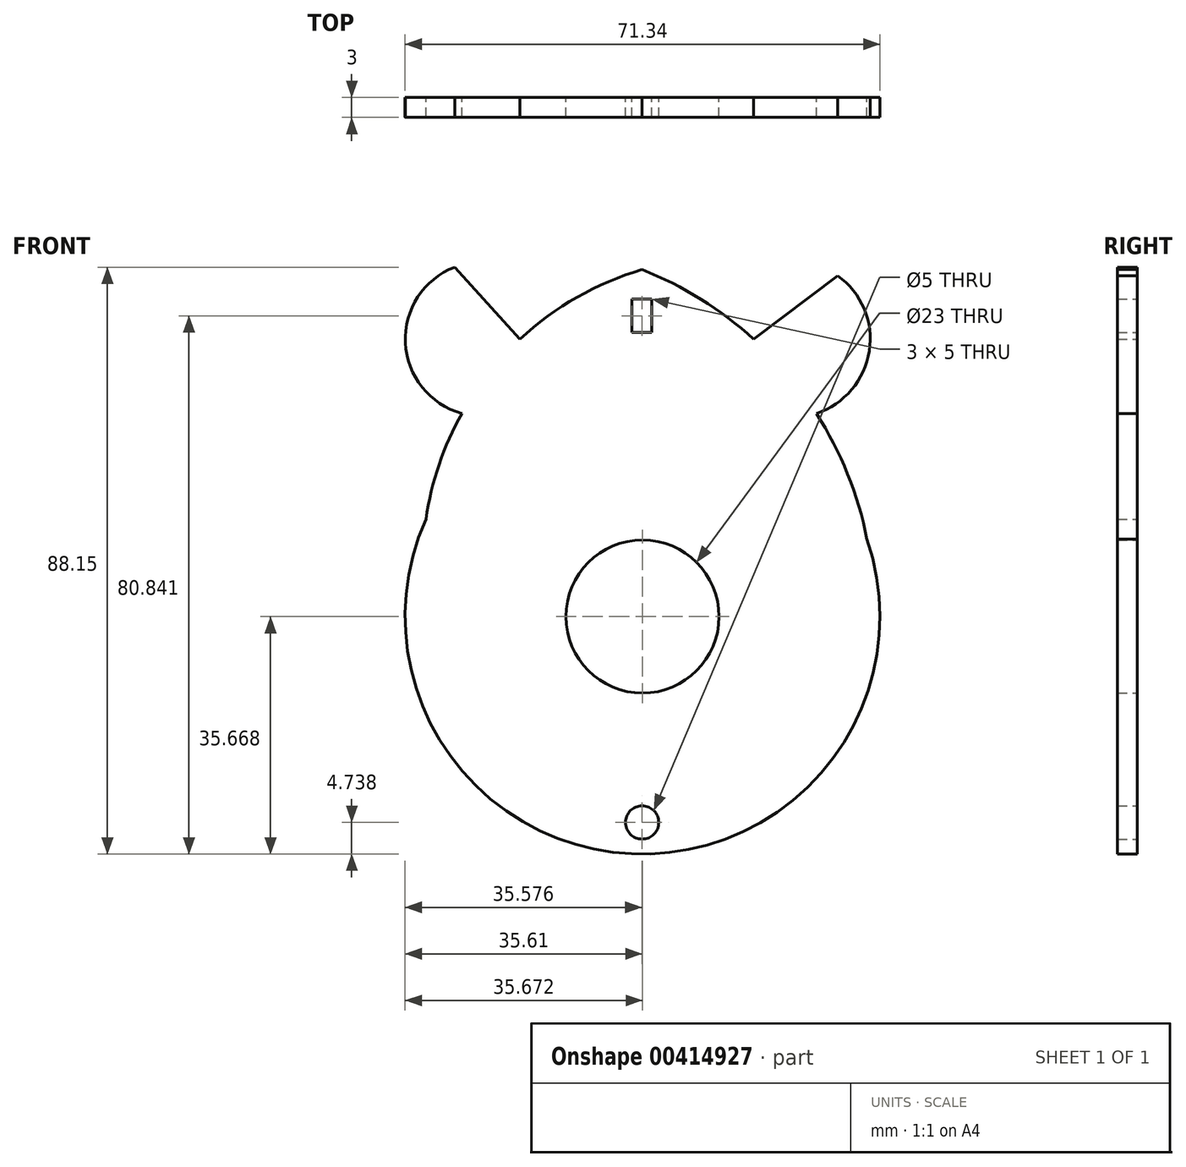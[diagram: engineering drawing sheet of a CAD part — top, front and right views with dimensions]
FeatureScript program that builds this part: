
annotation { "Feature Type Name" : "Feature", "Feature Type Description" : "" }
export const myFeature = defineFeature(function(context is Context, id is Id, definition is map)
    precondition{}
    {
        {
            var Q0;
            Q0=qCreatedBy(makeId("Front.planeOp"),FACE);
            var sketch = newSketch(context, id + "F0", { "sketchPlane" : qUnion([Q0])});
            skPoint(sketch, "E0.center.orphan", {"position": v(9.4, 0) * mm});
            skPoint(sketch, "E1.center.orphan", {"position": v(0, -6.4) * mm});
            skPoint(sketch, "E2.center.orphan", {"position": v(-9.91, 0) * mm});
            skArc(sketch, "E3", {"start": v(0, 72.4) * mm, "mid": v(-9.78, 68.25) * mm, "end": v(-18.34, 61.96) * mm});
            skArc(sketch, "E4", {"start": v(-32.47, 34.92) * mm, "mid": v(-1.57, -15.36) * mm, "end": v(33.8, 31.88) * mm});
            skArc(sketch, "E5.trimOffspring", {"start": v(33.8, 31.88) * mm, "mid": v(30.87, 41.7) * mm, "end": v(26.19, 50.8) * mm});
            skPoint(sketch, "E6.start.orphan", {"position": v(0, 68.22) * mm});
            skPoint(sketch, "E7.orphan", {"position": v(0, -10.65) * mm});
            skPoint(sketch, "E8.orphan", {"position": v(0, 28.79) * mm});
            skArc(sketch, "E9", {"start": v(-28.17, 72.76) * mm, "mid": v(-35.57, 61.4) * mm, "end": v(-27.1, 50.8) * mm});
            skArc(sketch, "E10", {"start": v(26.19, 50.8) * mm, "mid": v(34.14, 60.16) * mm, "end": v(29.4, 71.5) * mm});
            skLineSegment(sketch, "E11", {"start": v(16.76, 61.96) * mm, "end": v(29.4, 71.5) * mm});
            skLineSegment(sketch, "E12", {"start": v(-18.34, 61.96) * mm, "end": v(-28.17, 72.76) * mm});
            skPoint(sketch, "E13.start.orphan", {"position": v(0, 61.96) * mm});
            skCircle(sketch, "E14", {"center": v(0, -10.65) * mm, "radius": 2.5 * mm});
            skCircle(sketch, "E15", {"center": v(0.06, 20.28) * mm, "radius": 11.5 * mm});
            skArc(sketch, "E16.trimOffspring", {"start": v(16.76, 61.96) * mm, "mid": v(8.85, 67.94) * mm, "end": v(0, 72.4) * mm});
            skArc(sketch, "E17.trimOffspring", {"start": v(-27.1, 50.8) * mm, "mid": v(-30.51, 43.11) * mm, "end": v(-32.47, 34.92) * mm});
            skLineSegment(sketch, "E18", {"start": v(-1.53, 67.95) * mm, "end": v(1.47, 67.95) * mm});
            skLineSegment(sketch, "E19", {"start": v(-1.53, 67.95) * mm, "end": v(-1.53, 62.95) * mm});
            skLineSegment(sketch, "E20", {"start": v(1.47, 67.95) * mm, "end": v(1.47, 62.95) * mm});
            skLineSegment(sketch, "E21", {"start": v(-1.53, 62.95) * mm, "end": v(1.47, 62.95) * mm});
            skSolve(sketch);
        }
        {
            var Q0;
            Q0 = qSketchRegion(id + "F0", true);
            extrude(context, id + "F1", {"entities" : qUnion([Q0]), "depth" : 3 * mm});
        }
    });
